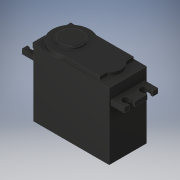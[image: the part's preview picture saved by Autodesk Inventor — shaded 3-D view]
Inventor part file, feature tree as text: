
AUTODESK INVENTOR PART (.ipt)
format: ipt  version: 2019 (Build 230136000, 136)  size: 149,504 bytes
history: native  units: mm
features: other x1, mirror x1
ambient origin geometry x8: Origin, YZ Plane, XZ Plane, XY Plane, X Axis, Y Axis, Z Axis, Center Point
bodies: Body1 (feature_tree)
feature tree (2):
  other  "Sólido1"
  mirror  "Mirror2"
